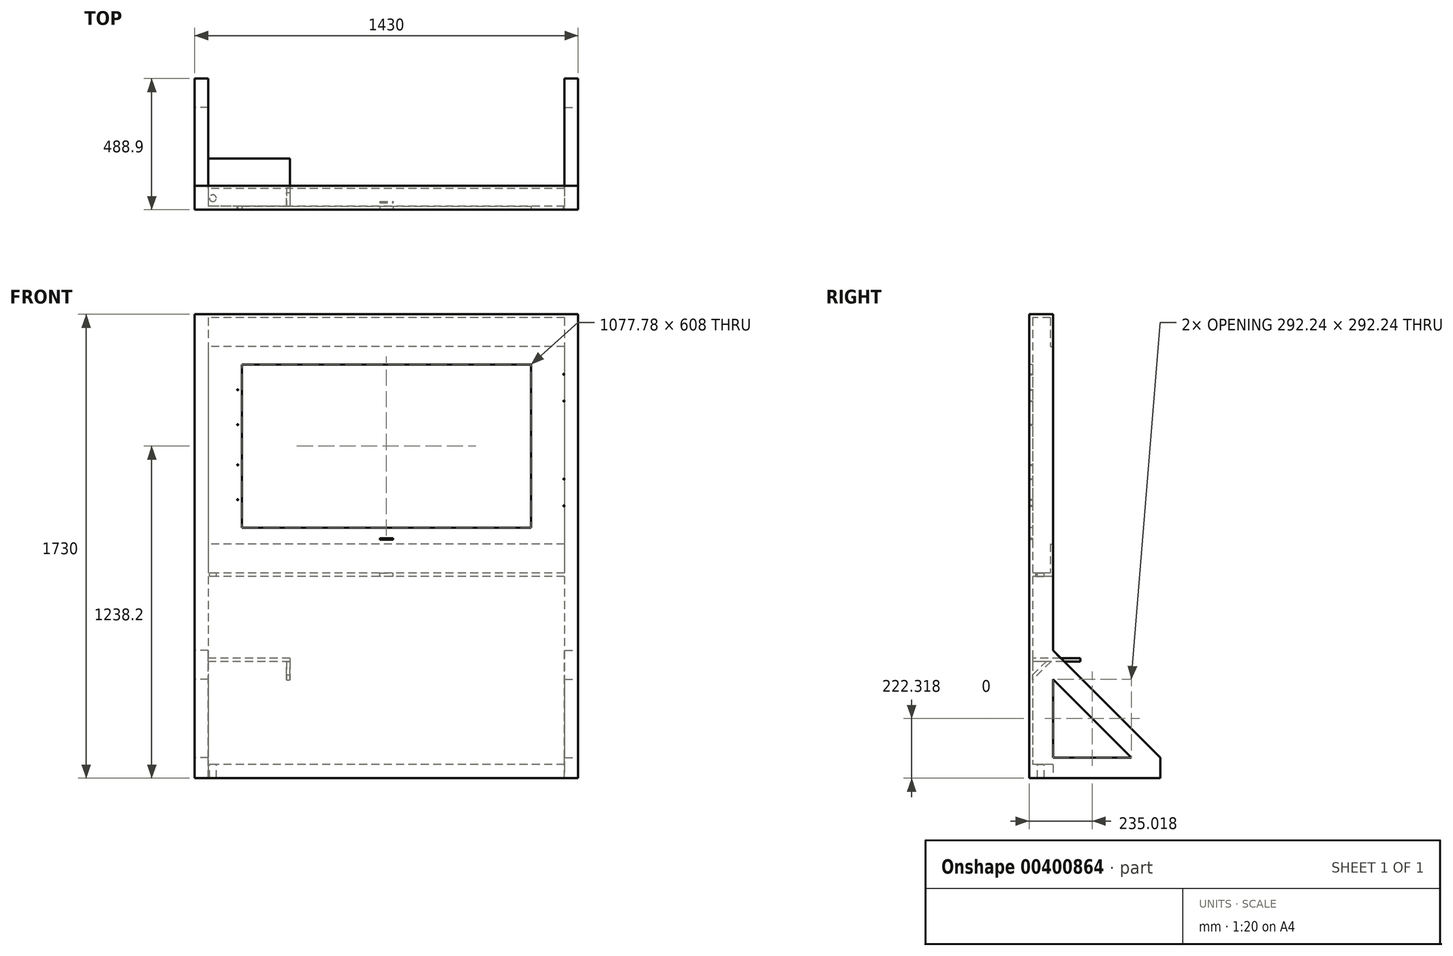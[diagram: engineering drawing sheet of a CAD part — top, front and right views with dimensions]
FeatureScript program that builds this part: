
annotation { "Feature Type Name" : "Feature", "Feature Type Description" : "" }
export const myFeature = defineFeature(function(context is Context, id is Id, definition is map)
    precondition{}
    {
        {
            var Q0;
            Q0=qCreatedBy(makeId("Front.planeOp"),FACE);
            var sketch = newSketch(context, id + "F0", { "sketchPlane" : qUnion([Q0])});
            skLineSegment(sketch, "E0.bottom", {"start": v(0, 1730) * mm, "end": v(1430, 1730) * mm});
            skLineSegment(sketch, "E0.top", {"start": v(0, 0) * mm, "end": v(1430, 0) * mm});
            skLineSegment(sketch, "E0.left", {"start": v(0, 1730) * mm, "end": v(0, 0) * mm});
            skLineSegment(sketch, "E0.right", {"start": v(1430, 1730) * mm, "end": v(1430, 0) * mm});
            skLineSegment(sketch, "E1.bottom", {"start": v(176.1, 1542.2) * mm, "end": v(1253.89, 1542.2) * mm});
            skLineSegment(sketch, "E1.top", {"start": v(176.11, 934.2) * mm, "end": v(1253.89, 934.2) * mm});
            skLineSegment(sketch, "E1.left", {"start": v(176.1, 1542.2) * mm, "end": v(176.1, 934.2) * mm});
            skLineSegment(sketch, "E1.right", {"start": v(1253.89, 1542.2) * mm, "end": v(1253.89, 934.2) * mm});
            skLineSegment(sketch, "E2", {"start": v(715, 1730) * mm, "end": v(715, 0) * mm, "construction": true});
            skLineSegment(sketch, "E3", {"start": v(176.1, 1238.2) * mm, "end": v(1253.89, 1238.2) * mm, "construction": true});
            skLineSegment(sketch, "E4.bottom", {"start": v(690, 894.2) * mm, "end": v(740, 894.2) * mm});
            skLineSegment(sketch, "E4.top", {"start": v(690, 889.2) * mm, "end": v(740, 889.2) * mm});
            skLineSegment(sketch, "E4.left", {"start": v(740, 894.2) * mm, "end": v(740, 889.2) * mm});
            skLineSegment(sketch, "E4.right", {"start": v(690, 894.2) * mm, "end": v(690, 889.2) * mm});
            skSolve(sketch);
        }
        {
            var Q0;
            Q0=makeQuery(id+"F0.imprint","IMPRINT",FACE,{"disambiguationData":[TD([[makeQuery(id+"F0.imprint","IMPRINT",EDGE,{"derivedFrom":sQuery(id+"F0.wireOp",EDGE,"E0.bottom")}),-1.0]])]});
            extrude(context, id + "F1", {"entities" : qUnion([Q0]), "oppositeDirection" : true, "depth" : 12.7 * mm});
        }
        {
            var Q0;
            Q0=makeQuery(id+"F1.opExtrude","CAP_FACE",FACE,{"disambiguationData":[OSD([sQuery(id+"F0.wireOp",EDGE,"E0.bottom"),sQuery(id+"F0.wireOp",EDGE,"E0.top"),sQuery(id+"F0.wireOp",EDGE,"E0.left"),sQuery(id+"F0.wireOp",EDGE,"E0.right"),sQuery(id+"F0.wireOp",EDGE,"E1.bottom"),sQuery(id+"F0.wireOp",EDGE,"E1.top"),sQuery(id+"F0.wireOp",EDGE,"E1.left"),sQuery(id+"F0.wireOp",EDGE,"E1.right")])],"isStart":false});
            var sketch = newSketch(context, id + "F2", { "sketchPlane" : qUnion([Q0])});
            skLineSegment(sketch, "E5.top", {"start": v(-1480.8, 0) * mm, "end": v(-1430, 0) * mm});
            skLineSegment(sketch, "E5.left", {"start": v(-1379.2, 1730) * mm, "end": v(-1379.2, 0) * mm});
            skLineSegment(sketch, "E5.right", {"start": v(-1430, 1730) * mm, "end": v(-1430, 0) * mm});
            skLineSegment(sketch, "E6", {"start": v(-715, 1730) * mm, "end": v(-715, 0) * mm});
            skLineSegment(sketch, "E7.MirrorCS", {"start": v(0, 1730) * mm, "end": v(-50.8, 1730) * mm});
            skLineSegment(sketch, "E8.MirrorCS", {"start": v(-50.8, 1730) * mm, "end": v(-50.8, 0) * mm});
            skLineSegment(sketch, "E9.MirrorCS", {"start": v(0, 1730) * mm, "end": v(0, 0) * mm});
            skLineSegment(sketch, "E10.MirrorCS", {"start": v(50.8, 0) * mm, "end": v(0, 0) * mm});
            skLineSegment(sketch, "E11", {"start": v(0, 865) * mm, "end": v(-1430, 865) * mm, "construction": true});
            skLineSegment(sketch, "E12.bottom", {"start": v(-1430, 1730) * mm, "end": v(0, 1730) * mm});
            skLineSegment(sketch, "E12.top", {"start": v(-1430, 1717.3) * mm, "end": v(0, 1717.3) * mm});
            skLineSegment(sketch, "E12.left", {"start": v(-1430, 1730) * mm, "end": v(-1430, 1717.3) * mm});
            skLineSegment(sketch, "E12.right", {"start": v(0, 1730) * mm, "end": v(0, 1717.3) * mm});
            skLineSegment(sketch, "E13.bottom", {"start": v(-1430, 50.8) * mm, "end": v(0, 50.8) * mm});
            skLineSegment(sketch, "E13.top", {"start": v(-1430, 0) * mm, "end": v(0, 0) * mm});
            skLineSegment(sketch, "E13.left", {"start": v(-1430, 50.8) * mm, "end": v(-1430, 0) * mm});
            skLineSegment(sketch, "E13.right", {"start": v(0, 50.8) * mm, "end": v(0, 0) * mm});
            skLineSegment(sketch, "E14.left", {"start": v(-1430, 737.95) * mm, "end": v(-1430, 718.9) * mm});
            skLineSegment(sketch, "E14.right", {"start": v(0, 737.95) * mm, "end": v(0, 718.9) * mm});
            skLineSegment(sketch, "E15", {"start": v(-1430, 1730) * mm, "end": v(-1379.2, 1730) * mm});
            skSolve(sketch);
        }
        {
            var Q0;
            Q0=qSketchRegion(id+"F2",true);
            extrude(context, id + "F3", {"entities" : qUnion([Q0]), "operationType" : NewBodyOperationType.ADD, "depth" : 76.2 * mm});
        }
        {
            var Q0;
            Q0=makeQuery(id+"F1.opExtrude","CAP_FACE",FACE,{"disambiguationData":[OSD([sQuery(id+"F0.wireOp",EDGE,"E0.bottom"),sQuery(id+"F0.wireOp",EDGE,"E0.top"),sQuery(id+"F0.wireOp",EDGE,"E0.left"),sQuery(id+"F0.wireOp",EDGE,"E0.right"),sQuery(id+"F0.wireOp",EDGE,"E1.bottom"),sQuery(id+"F0.wireOp",EDGE,"E1.top"),sQuery(id+"F0.wireOp",EDGE,"E1.left"),sQuery(id+"F0.wireOp",EDGE,"E1.right")])],"isStart":false});
            var sketch = newSketch(context, id + "F4", { "sketchPlane" : qUnion([Q0])});
            skLineSegment(sketch, "E16.bottom", {"start": v(-1379.2, 765.55) * mm, "end": v(-50.8, 765.55) * mm});
            skLineSegment(sketch, "E16.top", {"start": v(-1379.2, 752.85) * mm, "end": v(-50.8, 752.85) * mm});
            skLineSegment(sketch, "E16.left", {"start": v(-1379.2, 765.55) * mm, "end": v(-1379.2, 752.85) * mm});
            skLineSegment(sketch, "E16.right", {"start": v(-50.8, 765.55) * mm, "end": v(-50.8, 752.85) * mm});
            skPoint(sketch, "E17.orphan", {"position": v(-1379.2, 765.87) * mm});
            skSolve(sketch);
        }
        {
            var Q0;
            Q0=qSketchRegion(id+"F4",true);
            extrude(context, id + "F5", {"entities" : qUnion([Q0]), "operationType" : NewBodyOperationType.ADD, "depth" : 76.2 * mm});
        }
        {
            var Q0;
            Q0=makeQuery(id+"F5.boolean.opBoolean","MERGE",FACE,{"derivedFrom":[makeQuery(id+"F3.opExtrude","CAP_FACE",FACE,{"disambiguationData":[OSD([sQuery(id+"F2.wireOp",EDGE,"E5.top"),sQuery(id+"F2.wireOp",EDGE,"E5.left"),sQuery(id+"F2.wireOp",EDGE,"E5.right"),sQuery(id+"F2.wireOp",EDGE,"E7.MirrorCS"),sQuery(id+"F2.wireOp",EDGE,"E8.MirrorCS"),sQuery(id+"F2.wireOp",EDGE,"E9.MirrorCS"),sQuery(id+"F2.wireOp",EDGE,"E10.MirrorCS"),sQuery(id+"F2.wireOp",EDGE,"E12.bottom"),sQuery(id+"F2.wireOp",EDGE,"E12.top"),sQuery(id+"F2.wireOp",EDGE,"E13.bottom"),sQuery(id+"F2.wireOp",EDGE,"E13.top"),sQuery(id+"F2.wireOp",EDGE,"E14.left"),sQuery(id+"F2.wireOp",EDGE,"E14.right"),sQuery(id+"F2.wireOp",EDGE,"E15")])],"isStart":false}),makeQuery(id+"F5.opExtrude","CAP_FACE",FACE,{"disambiguationData":[OSD([sQuery(id+"F4.wireOp",EDGE,"E16.bottom"),sQuery(id+"F4.wireOp",EDGE,"E16.top"),sQuery(id+"F4.wireOp",EDGE,"E16.left"),sQuery(id+"F4.wireOp",EDGE,"E16.right")])],"isStart":false})]});
            var sketch = newSketch(context, id + "F6", { "sketchPlane" : qUnion([Q0])});
            skLineSegment(sketch, "E18.bottom", {"start": v(-1430, 1730) * mm, "end": v(-50.8, 1730) * mm});
            skLineSegment(sketch, "E18.top", {"start": v(-1430, 1609.35) * mm, "end": v(-50.8, 1609.35) * mm});
            skLineSegment(sketch, "E18.left", {"start": v(-1430, 1730) * mm, "end": v(-1430, 1609.35) * mm});
            skLineSegment(sketch, "E18.right", {"start": v(-50.8, 1730) * mm, "end": v(-50.8, 1609.35) * mm});
            skLineSegment(sketch, "E19", {"start": v(-1430, 865) * mm, "end": v(0, 865) * mm, "construction": true});
            skLineSegment(sketch, "E20.MirrorCS", {"start": v(-1380, 873.5) * mm, "end": v(-50.8, 873.5) * mm});
            skLineSegment(sketch, "E21.MirrorCS", {"start": v(-1380, 752.85) * mm, "end": v(-50.8, 752.85) * mm});
            skLineSegment(sketch, "E22.MirrorCS", {"start": v(-1380, 765.5) * mm, "end": v(-1380, 873.5) * mm});
            skLineSegment(sketch, "E23.MirrorCS", {"start": v(-50.8, 765.5) * mm, "end": v(-50.8, 873.5) * mm});
            skSolve(sketch);
        }
        {
            var Q0;
            Q0=qSketchRegion(id+"F6",true);
            var Q1;
            {var subQ2=sQuery(id+"F4.wireOp",EDGE,"E16.bottom");var subQ13=makeQuery(id+"F5.opExtrude","CAP_EDGE",EDGE,{"disambiguationData":[OSD([subQ2])],"isStart":false});Q1=makeQuery(id+"F6.imprint","IMPRINT",FACE,{"disambiguationData":[TD([[makeQuery(id+"F6.imprint","IMPRINT",EDGE,{"derivedFrom":subQ13}),1.0]])]});}
            extrude(context, id + "F7", {"entities" : qUnion([Q0, Q1]), "operationType" : NewBodyOperationType.ADD, "oppositeDirection" : true, "depth" : 9.53 * mm});
        }
        {
            var Q0;
            Q0=makeQuery(id+"F3.boolean.opBoolean","MERGE",FACE,{"derivedFrom":[makeQuery(id+"F1.opExtrude","SWEPT_FACE",FACE,{"disambiguationData":[OSD([sQuery(id+"F0.wireOp",EDGE,"E0.right")])]}),makeQuery(id+"F3.opExtrude","SWEPT_FACE",FACE,{"disambiguationData":[OSD([sQuery(id+"F2.wireOp",EDGE,"E5.left")])]})]});
            var sketch = newSketch(context, id + "F8", { "sketchPlane" : qUnion([Q0])});
            skLineSegment(sketch, "E24.bottom", {"start": v(88.9, 0) * mm, "end": v(488.9, 0) * mm});
            skLineSegment(sketch, "E24.top", {"start": v(88.9, 76.2) * mm, "end": v(488.9, 76.2) * mm});
            skLineSegment(sketch, "E24.left", {"start": v(88.9, 0) * mm, "end": v(88.9, 76.2) * mm});
            skLineSegment(sketch, "E24.right", {"start": v(488.9, 0) * mm, "end": v(488.9, 76.2) * mm});
            skSolve(sketch);
        }
        {
            var Q0;
            Q0=qSketchRegion(id+"F8",true);
            extrude(context, id + "F9", {"entities" : qUnion([Q0]), "operationType" : NewBodyOperationType.ADD, "oppositeDirection" : true, "depth" : 50.8 * mm});
        }
        {
            var Q0;
            Q0=makeQuery(id+"F9.boolean.opBoolean","MERGE",FACE,{"derivedFrom":[makeQuery(id+"F3.boolean.opBoolean","MERGE",FACE,{"derivedFrom":[makeQuery(id+"F1.opExtrude","SWEPT_FACE",FACE,{"disambiguationData":[OSD([sQuery(id+"F0.wireOp",EDGE,"E0.right")])]}),makeQuery(id+"F3.opExtrude","SWEPT_FACE",FACE,{"disambiguationData":[OSD([sQuery(id+"F2.wireOp",EDGE,"E5.left")])]})]}),makeQuery(id+"F9.opExtrude","CAP_FACE",FACE,{"disambiguationData":[OSD([sQuery(id+"F8.wireOp",EDGE,"E24.bottom"),sQuery(id+"F8.wireOp",EDGE,"E24.top"),sQuery(id+"F8.wireOp",EDGE,"E24.left"),sQuery(id+"F8.wireOp",EDGE,"E24.right")])],"isStart":true})]});
            var sketch = newSketch(context, id + "F10", { "sketchPlane" : qUnion([Q0])});
            skLineSegment(sketch, "E25", {"start": v(488.9, 76.2) * mm, "end": v(88.9, 476.2) * mm});
            skLineSegment(sketch, "E26.0", {"start": v(381.14, 76.2) * mm, "end": v(88.9, 368.44) * mm});
            skLineSegment(sketch, "E27", {"start": v(88.9, 476.2) * mm, "end": v(88.9, 368.44) * mm});
            skLineSegment(sketch, "E28", {"start": v(381.14, 76.2) * mm, "end": v(488.9, 76.2) * mm});
            skSolve(sketch);
        }
        {
            var Q0;
            Q0=qSketchRegion(id+"F10",true);
            extrude(context, id + "F11", {"entities" : qUnion([Q0]), "operationType" : NewBodyOperationType.ADD, "oppositeDirection" : true, "depth" : 50.8 * mm});
        }
        {
            var Q0;
            Q0=makeQuery(id+"F5.opExtrude","SWEPT_FACE",FACE,{"disambiguationData":[OSD([sQuery(id+"F4.wireOp",EDGE,"E16.bottom")])]});
            var sketch = newSketch(context, id + "F12", { "sketchPlane" : qUnion([Q0])});
            skCircle(sketch, "E29", {"center": v(67.7, 42.86) * mm, "radius": 12.7 * mm});
            skLineSegment(sketch, "E30.bottom", {"start": v(690, 30) * mm, "end": v(740, 30) * mm});
            skLineSegment(sketch, "E30.top", {"start": v(690, 25) * mm, "end": v(740, 25) * mm});
            skLineSegment(sketch, "E30.left", {"start": v(690, 30) * mm, "end": v(690, 25) * mm});
            skLineSegment(sketch, "E30.right", {"start": v(740, 30) * mm, "end": v(740, 25) * mm});
            skPoint(sketch, "E30.middle", {"position": v(715, 27.5) * mm});
            skPoint(sketch, "E30.middle.positionSnap0", {"position": v(715, 12.7) * mm});
            skPoint(sketch, "E30.centerSnap0", {"position": v(715, 12.7) * mm});
            skSolve(sketch);
        }
        {
            var Q0;
            Q0=qSketchRegion(id+"F12",true);
            extrude(context, id + "F13", {"entities" : qUnion([Q0]), "operationType" : NewBodyOperationType.REMOVE, "endBound" : BoundingType.UP_TO_NEXT, "oppositeDirection" : true, "depth" : 25 * mm});
        }
        {
            var Q0;
            Q0=makeQuery(id+"F3.opExtrude","SWEPT_FACE",FACE,{"disambiguationData":[OSD([sQuery(id+"F2.wireOp",EDGE,"E13.bottom")])]});
            var sketch = newSketch(context, id + "F14", { "sketchPlane" : qUnion([Q0])});
            skCircle(sketch, "E31", {"center": v(67.7, 42.86) * mm, "radius": 12.7 * mm});
            skPoint(sketch, "E31.centerSnap0", {"position": v(50.8, 57.15) * mm});
            skSolve(sketch);
        }
        {
            var Q0;
            Q0=makeQuery(id+"F3.boolean.opBoolean","MERGE",FACE,{"derivedFrom":[makeQuery(id+"F1.opExtrude","SWEPT_FACE",FACE,{"disambiguationData":[OSD([sQuery(id+"F0.wireOp",EDGE,"E0.left")])]}),makeQuery(id+"F3.opExtrude","SWEPT_FACE",FACE,{"disambiguationData":[OSD([sQuery(id+"F2.wireOp",EDGE,"E8.MirrorCS")])]})]});
            var sketch = newSketch(context, id + "F15", { "sketchPlane" : qUnion([Q0])});
            skLineSegment(sketch, "E32.bottom", {"start": v(-88.9, 0) * mm, "end": v(-488.9, 0) * mm});
            skLineSegment(sketch, "E32.top", {"start": v(-88.9, 76.2) * mm, "end": v(-488.9, 76.2) * mm});
            skLineSegment(sketch, "E32.left", {"start": v(-88.9, 0) * mm, "end": v(-88.9, 76.2) * mm});
            skLineSegment(sketch, "E32.right", {"start": v(-488.9, 0) * mm, "end": v(-488.9, 76.2) * mm});
            skSolve(sketch);
        }
        {
            var Q0;
            Q0=qSketchRegion(id+"F15",true);
            extrude(context, id + "F16", {"entities" : qUnion([Q0]), "operationType" : NewBodyOperationType.ADD, "oppositeDirection" : true, "depth" : 50.8 * mm});
        }
        {
            var Q0;
            Q0=makeQuery(id+"F16.boolean.opBoolean","MERGE",FACE,{"derivedFrom":[makeQuery(id+"F3.boolean.opBoolean","MERGE",FACE,{"derivedFrom":[makeQuery(id+"F1.opExtrude","SWEPT_FACE",FACE,{"disambiguationData":[OSD([sQuery(id+"F0.wireOp",EDGE,"E0.left")])]}),makeQuery(id+"F3.opExtrude","SWEPT_FACE",FACE,{"disambiguationData":[OSD([sQuery(id+"F2.wireOp",EDGE,"E8.MirrorCS")])]})]}),makeQuery(id+"F16.opExtrude","CAP_FACE",FACE,{"disambiguationData":[OSD([sQuery(id+"F15.wireOp",EDGE,"E32.bottom"),sQuery(id+"F15.wireOp",EDGE,"E32.top"),sQuery(id+"F15.wireOp",EDGE,"E32.left"),sQuery(id+"F15.wireOp",EDGE,"E32.right")])],"isStart":true})]});
            var sketch = newSketch(context, id + "F17", { "sketchPlane" : qUnion([Q0])});
            skLineSegment(sketch, "E33", {"start": v(-488.9, 76.2) * mm, "end": v(-88.9, 476.2) * mm});
            skLineSegment(sketch, "E34.0", {"start": v(-381.14, 76.2) * mm, "end": v(-88.9, 368.44) * mm});
            skLineSegment(sketch, "E35", {"start": v(-88.9, 476.2) * mm, "end": v(-88.9, 368.44) * mm});
            skLineSegment(sketch, "E36", {"start": v(-488.9, 76.2) * mm, "end": v(-381.14, 76.2) * mm});
            skSolve(sketch);
        }
        {
            var Q0;
            Q0=makeQuery(id+"F17.imprint","IMPRINT",FACE,{"disambiguationData":[TD([[makeQuery(id+"F17.imprint","IMPRINT",EDGE,{"derivedFrom":sQuery(id+"F17.wireOp",EDGE,"E33")}),-1.0]])]});
            extrude(context, id + "F18", {"entities" : qUnion([Q0]), "operationType" : NewBodyOperationType.ADD, "oppositeDirection" : true, "depth" : 50.8 * mm});
        }
        {
            var Q0;
            {var subQ0=sQuery(id+"F0.wireOp",EDGE,"E1.left");var subQ1=sQuery(id+"F0.wireOp",EDGE,"E4.right");var subQ2=sQuery(id+"F0.wireOp",EDGE,"E4.left");var subQ3=sQuery(id+"F0.wireOp",EDGE,"E4.top");var subQ4=sQuery(id+"F0.wireOp",EDGE,"E4.bottom");var subQ5=sQuery(id+"F0.wireOp",EDGE,"E1.bottom");var subQ6=sQuery(id+"F0.wireOp",EDGE,"E1.top");var subQ7=sQuery(id+"F0.wireOp",EDGE,"E1.right");Q0=makeQuery(id+"F5.boolean.opBoolean","SPLIT",FACE,{"disambiguationData":[TD([makeQuery(id+"F1.opExtrude","SWEPT_FACE",FACE,{"disambiguationData":[OSD([subQ5])]})])],"derivedFrom":makeQuery(id+"F1.opExtrude","CAP_FACE",FACE,{"disambiguationData":[OSD([sQuery(id+"F0.wireOp",EDGE,"E0.bottom"),sQuery(id+"F0.wireOp",EDGE,"E0.top"),sQuery(id+"F0.wireOp",EDGE,"E0.left"),sQuery(id+"F0.wireOp",EDGE,"E0.right"),subQ5,subQ6,subQ0,subQ7,subQ4,subQ3,subQ2,subQ1])],"isStart":false})});}
            var sketch = newSketch(context, id + "F19", { "sketchPlane" : qUnion([Q0])});
            skLineSegment(sketch, "E37.bottom", {"start": v(-157.41, 1606.3) * mm, "end": v(-1379.75, 1606.3) * mm, "construction": true});
            skLineSegment(sketch, "E37.top", {"start": v(-157.4, 915.5) * mm, "end": v(-1379.75, 915.5) * mm, "construction": true});
            skLineSegment(sketch, "E37.left", {"start": v(-157.41, 1606.3) * mm, "end": v(-157.4, 915.5) * mm, "construction": true});
            skLineSegment(sketch, "E37.right", {"start": v(-1379.75, 1606.3) * mm, "end": v(-1379.75, 915.5) * mm, "construction": true});
            skPoint(sketch, "E37.middle", {"position": v(-768.58, 1260.9) * mm});
            skLineSegment(sketch, "E38", {"start": v(-1379.75, 1606.3) * mm, "end": v(-1379.2, 1506.3) * mm, "construction": true});
            skLineSegment(sketch, "E39", {"start": v(-1379.2, 1506.3) * mm, "end": v(-1376.2, 1506.32) * mm, "construction": true});
            skLineSegment(sketch, "E40", {"start": v(-1379.2, 1506.3) * mm, "end": v(-1379.75, 1406.3) * mm, "construction": true});
            skLineSegment(sketch, "E41", {"start": v(-1379.75, 1406.3) * mm, "end": v(-1376.75, 1406.29) * mm, "construction": true});
            skCircle(sketch, "E42", {"center": v(-1376.75, 1406.29) * mm, "radius": 1.75 * mm});
            skCircle(sketch, "E43", {"center": v(-1376.2, 1506.32) * mm, "radius": 1.75 * mm});
            skLineSegment(sketch, "E44", {"start": v(-1379.75, 915.5) * mm, "end": v(-1379.75, 1015.5) * mm, "construction": true});
            skLineSegment(sketch, "E45", {"start": v(-1379.75, 1015.5) * mm, "end": v(-1379.75, 1115.5) * mm, "construction": true});
            skLineSegment(sketch, "E46", {"start": v(-1379.75, 1115.5) * mm, "end": v(-1376.75, 1115.5) * mm, "construction": true});
            skLineSegment(sketch, "E47", {"start": v(-1379.75, 1015.5) * mm, "end": v(-1376.75, 1015.5) * mm, "construction": true});
            skCircle(sketch, "E48", {"center": v(-1376.75, 1115.5) * mm, "radius": 1.75 * mm});
            skCircle(sketch, "E49", {"center": v(-1376.75, 1015.5) * mm, "radius": 1.75 * mm});
            skLineSegment(sketch, "E50", {"start": v(-157.41, 1606.3) * mm, "end": v(-157.41, 1448.3) * mm, "construction": true});
            skLineSegment(sketch, "E51", {"start": v(-157.41, 1448.3) * mm, "end": v(-157.41, 1318.3) * mm, "construction": true});
            skLineSegment(sketch, "E52", {"start": v(-157.41, 1448.3) * mm, "end": v(-160.41, 1448.3) * mm, "construction": true});
            skLineSegment(sketch, "E53", {"start": v(-157.41, 1318.3) * mm, "end": v(-160.4, 1318.3) * mm, "construction": true});
            skCircle(sketch, "E54", {"center": v(-160.41, 1448.3) * mm, "radius": 1.75 * mm});
            skCircle(sketch, "E55", {"center": v(-160.4, 1318.3) * mm, "radius": 1.75 * mm});
            skLineSegment(sketch, "E56", {"start": v(-157.4, 915.5) * mm, "end": v(-157.41, 1038.3) * mm, "construction": true});
            skLineSegment(sketch, "E57", {"start": v(-157.41, 1038.3) * mm, "end": v(-157.4, 1168.3) * mm, "construction": true});
            skLineSegment(sketch, "E58", {"start": v(-157.4, 1168.3) * mm, "end": v(-160.4, 1168.3) * mm, "construction": true});
            skLineSegment(sketch, "E59", {"start": v(-157.41, 1038.3) * mm, "end": v(-160.4, 1038.3) * mm, "construction": true});
            skCircle(sketch, "E60", {"center": v(-160.4, 1168.3) * mm, "radius": 1.75 * mm});
            skCircle(sketch, "E61", {"center": v(-160.4, 1038.3) * mm, "radius": 1.75 * mm});
            skSolve(sketch);
        }
        {
            var Q0;
            Q0=qSketchRegion(id+"F19",true);
            extrude(context, id + "F20", {"entities" : qUnion([Q0]), "operationType" : NewBodyOperationType.REMOVE, "endBound" : BoundingType.THROUGH_ALL, "oppositeDirection" : true, "depth" : 25 * mm});
        }
        {
            var Q0;
            Q0=qSketchRegion(id+"F14",true);
            extrude(context, id + "F21", {"entities" : qUnion([Q0]), "operationType" : NewBodyOperationType.REMOVE, "endBound" : BoundingType.THROUGH_ALL, "oppositeDirection" : true, "depth" : 25 * mm});
        }
        {
            var Q0;
            Q0=makeQuery(id+"F5.boolean.opBoolean","SPLIT",FACE,{"disambiguationData":[TD([makeQuery(id+"F3.opExtrude","SWEPT_FACE",FACE,{"disambiguationData":[OSD([sQuery(id+"F2.wireOp",EDGE,"E13.bottom")])]})])],"derivedFrom":makeQuery(id+"F1.opExtrude","CAP_FACE",FACE,{"disambiguationData":[OSD([sQuery(id+"F0.wireOp",EDGE,"E0.bottom"),sQuery(id+"F0.wireOp",EDGE,"E0.top"),sQuery(id+"F0.wireOp",EDGE,"E0.left"),sQuery(id+"F0.wireOp",EDGE,"E0.right"),sQuery(id+"F0.wireOp",EDGE,"E1.bottom"),sQuery(id+"F0.wireOp",EDGE,"E1.top"),sQuery(id+"F0.wireOp",EDGE,"E1.left"),sQuery(id+"F0.wireOp",EDGE,"E1.right"),sQuery(id+"F0.wireOp",EDGE,"E4.bottom"),sQuery(id+"F0.wireOp",EDGE,"E4.top"),sQuery(id+"F0.wireOp",EDGE,"E4.left"),sQuery(id+"F0.wireOp",EDGE,"E4.right")])],"isStart":false})});
            var sketch = newSketch(context, id + "F22", { "sketchPlane" : qUnion([Q0])});
            skLineSegment(sketch, "E62.bottom", {"start": v(-355.6, 448.05) * mm, "end": v(-50.8, 448.05) * mm});
            skLineSegment(sketch, "E62.top", {"start": v(-355.6, 435.35) * mm, "end": v(-50.8, 435.35) * mm});
            skLineSegment(sketch, "E62.left", {"start": v(-355.6, 448.05) * mm, "end": v(-355.6, 435.35) * mm});
            skLineSegment(sketch, "E62.right", {"start": v(-50.8, 448.05) * mm, "end": v(-50.8, 435.35) * mm});
            skSolve(sketch);
        }
        {
            var Q0;
            Q0=makeQuery(id+"F22.imprint","IMPRINT",FACE,{"disambiguationData":[TD([[makeQuery(id+"F22.imprint","IMPRINT",EDGE,{"derivedFrom":sQuery(id+"F22.wireOp",EDGE,"E62.bottom")}),-1.0]])]});
            extrude(context, id + "F23", {"entities" : qUnion([Q0]), "operationType" : NewBodyOperationType.ADD, "depth" : 177.8 * mm});
        }
        {
            var Q0;
            Q0=makeQuery(id+"F23.opExtrude","SWEPT_FACE",FACE,{"disambiguationData":[OSD([sQuery(id+"F22.wireOp",EDGE,"E62.left")])]});
            var sketch = newSketch(context, id + "F24", { "sketchPlane" : qUnion([Q0])});
            skLineSegment(sketch, "E63", {"start": v(63.22, 435.35) * mm, "end": v(81.02, 435.35) * mm});
            skLineSegment(sketch, "E64", {"start": v(12.7, 375.85) * mm, "end": v(12.7, 384.83) * mm});
            skLineSegment(sketch, "E65", {"start": v(12.7, 384.83) * mm, "end": v(12.7, 375.85) * mm});
            skLineSegment(sketch, "E66", {"start": v(12.7, 375.85) * mm, "end": v(12.7, 366.87) * mm});
            skLineSegment(sketch, "E67", {"start": v(81.02, 435.35) * mm, "end": v(12.7, 366.87) * mm});
            skLineSegment(sketch, "E68", {"start": v(12.7, 384.83) * mm, "end": v(63.22, 435.35) * mm});
            skSolve(sketch);
        }
        {
            var Q0;
            Q0=makeQuery(id+"F24.imprint","IMPRINT",FACE,{"disambiguationData":[TD([[makeQuery(id+"F24.imprint","IMPRINT",EDGE,{"derivedFrom":sQuery(id+"F24.wireOp",EDGE,"E63")}),1.0]])]});
            extrude(context, id + "F25", {"entities" : qUnion([Q0]), "operationType" : NewBodyOperationType.ADD, "oppositeDirection" : true, "depth" : 12.7 * mm});
        }
    });
